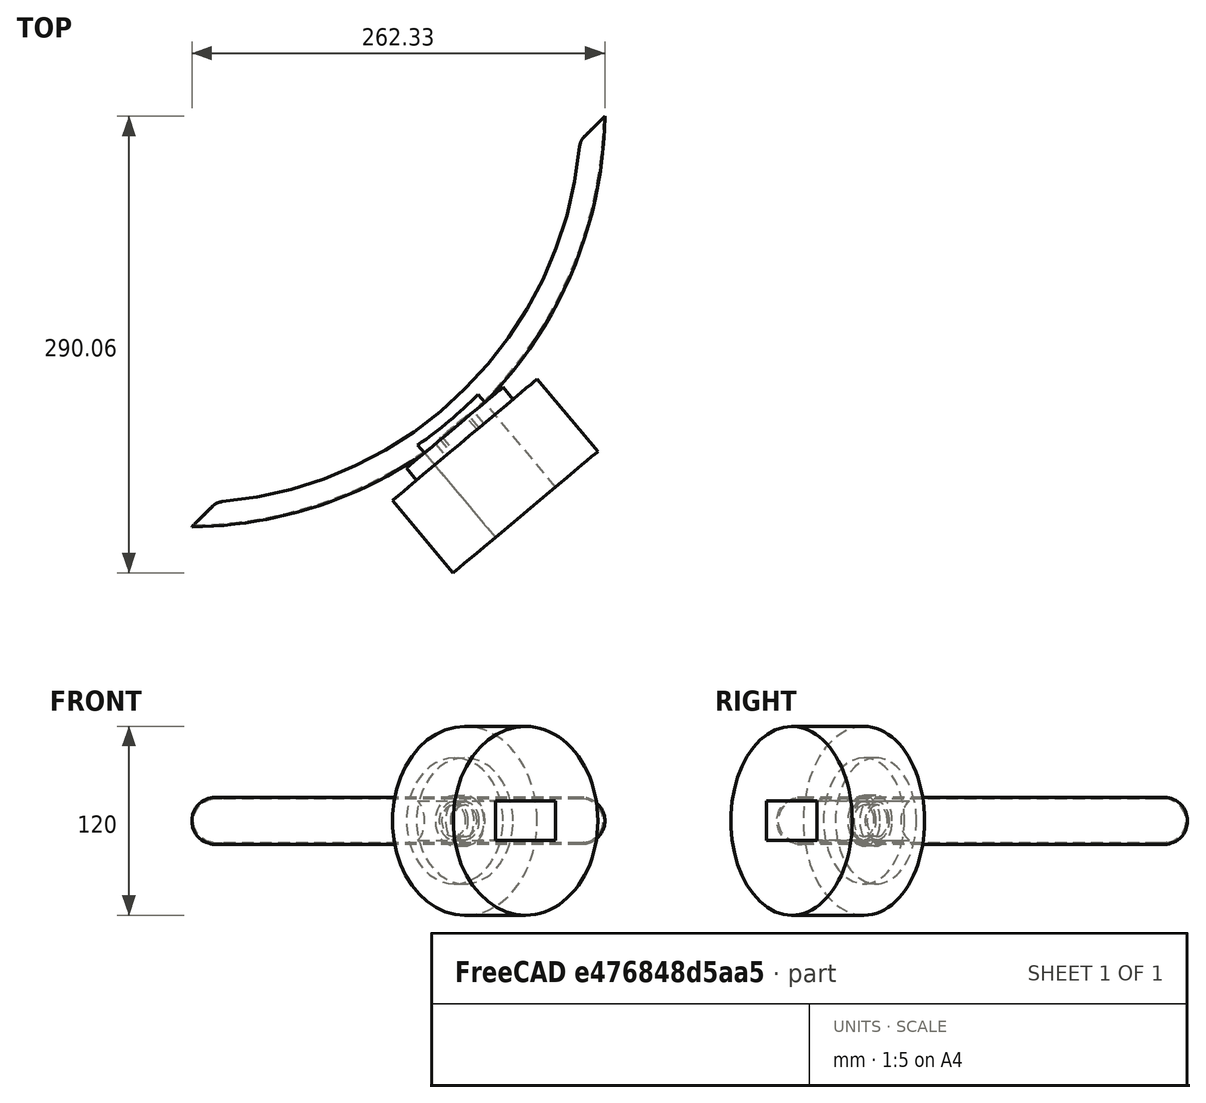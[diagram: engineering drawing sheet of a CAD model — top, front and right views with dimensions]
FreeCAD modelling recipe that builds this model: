
FCSTD DOCUMENT  (FreeCAD 0.16R)
Label: Mudguard2.1
License: All rights reserved
LicenseURL: http://en.wikipedia.org/wiki/All_rights_reserved
objects: Sketcher::SketchObject×6, PartDesign::Pocket×3, PartDesign::Pad×2, PartDesign::Revolution×1, Part::Cut×1, PartDesign::Fillet×1, Part::FeaturePython×1, Mesh::Feature×1
note: 21 computed .brp shape members not serialized (recipe doc carries the construction recipe); baked Part::Feature solids carry a one-line shape summary decoded from their .brp

FEATURE [Sketcher::SketchObject] Sketch001
  Placement = pos=(0,0,0) rot=(1,0,0;1.5708rad)
  sketch-geometry (4):
    g0: ArcOfCircle CenterX=250 CenterY=0 CenterZ=0 NormalX=0 NormalY=0 NormalZ=1 Radius=15 StartAngle=4.71239 EndAngle=7.85398
    g1: ArcOfCircle CenterX=250 CenterY=0 CenterZ=0 NormalX=0 NormalY=0 NormalZ=1 Radius=14 StartAngle=4.71239 EndAngle=7.85398
    g2: LineSegment StartX=250 StartY=15 StartZ=0 EndX=250 EndY=14 EndZ=0
    g3: LineSegment StartX=250 StartY=-15 StartZ=0 EndX=250 EndY=-14 EndZ=0
  constraints (13):
    c: DistanceX(g0,g-1) = -250
    c: Radius(g0) = 15
    c: PointOnObject(g0,g-1)
    c: Symmetric(g0,g0,g0)
    c: Coincident(g1,g0)
    c: Radius(g1) = 14
    c: DistanceX(g1) = 250
    c: DistanceX(g1) = 250
    c: Coincident(g2,g0)
    c: Coincident(g2,g1)
    c: Vertical(g2)
    c: Coincident(g3,g0)
    c: Coincident(g3,g1)
FEATURE [PartDesign::Revolution] Revolution
  Angle = 90
  Axis = (0,0,1)
  Base = (0,0,0)
  Placement = pos=(0,0,0) rot=(1,0,0;1.5708rad)
  ReferenceAxis = -> Sketch001 [V_Axis]
  Reversed = true
  Sketch = -> Sketch001
FEATURE [Sketcher::SketchObject] Sketch002
  sketch-geometry (3):
    g0: LineSegment StartX=307.15 StartY=37.7434 StartZ=0 EndX=-27.9422 EndY=-295.389 EndZ=0
    g1: LineSegment StartX=-27.9422 StartY=-295.389 StartZ=0 EndX=4.8812 EndY=80.7716 EndZ=0
    g2: LineSegment StartX=4.8812 StartY=80.7716 StartZ=0 EndX=307.15 EndY=37.7434 EndZ=0
  constraints (9):
    c: Coincident(g0,g1)
    c: Coincident(g1,g2)
    c: Coincident(g2,g0)
    c: DistanceX(g0) = 307.15
    c: DistanceY(g0) = 37.7434
    c: DistanceY(g0) = -295.389
    c: DistanceX(g0) = -27.9422
    c: Distance(g1) = 377.59
    c: Distance(g2) = 305.316
FEATURE [PartDesign::Pad] Pad
  Length = 40
  Length2 = 100
  Midplane = true
  Sketch = -> Sketch002
  Type = 0
FEATURE [Part::Cut] Cut
  Base = -> Revolution
  Tool = -> Pad
FEATURE [PartDesign::Fillet] Fillet
  Base = -> Cut [Edge7,Edge5,Edge11,Edge9]
  Radius = 10
FEATURE [Sketcher::SketchObject] Sketch003
  sketch-geometry (5):
    g0: LineSegment [constr] StartX=0 StartY=0 StartZ=0 EndX=352.662 EndY=-420.286 EndZ=0
    g1: LineSegment StartX=182.272 StartY=-178.331 StartZ=0 EndX=143.97 EndY=-210.47 EndZ=0
    g2: LineSegment StartX=143.97 StartY=-210.47 StartZ=0 EndX=195.393 EndY=-271.754 EndZ=0
    g3: LineSegment StartX=195.393 StartY=-271.754 StartZ=0 EndX=233.695 EndY=-239.614 EndZ=0
    g4: LineSegment StartX=233.695 StartY=-239.614 StartZ=0 EndX=182.272 EndY=-178.331 EndZ=0
  constraints (13):
    c: Coincident(g0,g-1)
    c: Angle(g0) = -0.872665
    c: Coincident(g1,g2)
    c: Coincident(g2,g3)
    c: Coincident(g3,g4)
    c: Coincident(g4,g1)
    c: Perpendicular(g0,g1)
    c: Parallel(g2,g4)
    c: Symmetric(g3,g2,g0)
    c: Distance(g2) = 80
    c: Distance(g3) = 50
    c: Symmetric(g1,g1,g0)
    c: Distance(g-1,g1) = 255
FEATURE [PartDesign::Pad] Pad001
  Length = 25
  Length2 = 100
  Midplane = true
  Sketch = -> Sketch003
  Type = 0
FEATURE [Part::FeaturePython] Connect  # WARN: FeaturePython — macro-defined, semantics opaque (R4)
  Base = -> Pad001
  Mode = 1
  Tool = -> Fillet
FEATURE [Sketcher::SketchObject] Sketch
  Placement = pos=(214.544,-255.684,0) rot=(0.889126,0.323616,0.323616;1.68804rad)
  Support = -> Connect [Face1]
  sketch-geometry (1):
    g0: Circle CenterX=0 CenterY=0 CenterZ=0 NormalX=0 NormalY=0 NormalZ=1 Radius=60
  constraints (2):
    c: Coincident(g0,g-1)
    c: Radius(g0) = 60
FEATURE [PartDesign::Pocket] Pocket
  Length = 60
  Sketch = -> Sketch
  Type = 0
FEATURE [Sketcher::SketchObject] Sketch004
  Placement = pos=(175.977,-209.721,0) rot=(0.889126,0.323616,0.323616;1.68804rad)
  Support = -> Pocket [Face3]
  sketch-geometry (2):
    g0: Circle CenterX=0 CenterY=0 CenterZ=0 NormalX=0 NormalY=0 NormalZ=1 Radius=10
    g1: Circle CenterX=0 CenterY=0 CenterZ=0 NormalX=0 NormalY=0 NormalZ=1 Radius=12
  constraints (4):
    c: Coincident(g0,g-1)
    c: Radius(g0) = 10
    c: Coincident(g1,g-1)
    c: Radius(g1) = 12
FEATURE [PartDesign::Pocket] Pocket001
  Length = 11
  Sketch = -> Sketch004
  Type = 0
FEATURE [Sketcher::SketchObject] Sketch005
  Placement = pos=(175.977,-209.721,0) rot=(0.889126,0.323616,0.323616;1.68804rad)
  Support = -> Pocket001 [Face3]
  sketch-geometry (2):
    g0: Circle CenterX=0 CenterY=0 CenterZ=0 NormalX=0 NormalY=0 NormalZ=1 Radius=16
    g1: Circle CenterX=0 CenterY=0 CenterZ=0 NormalX=0 NormalY=0 NormalZ=1 Radius=40
  constraints (4):
    c: Coincident(g0,g-1)
    c: Coincident(g1,g-1)
    c: Radius(g0) = 16
    c: Radius(g1) = 40
FEATURE [PartDesign::Pocket] Pocket002
  Length = 10
  Sketch = -> Sketch005
  Type = 0
FEATURE [Mesh::Feature] Mesh  label="Pocket002 (Meshed)"
